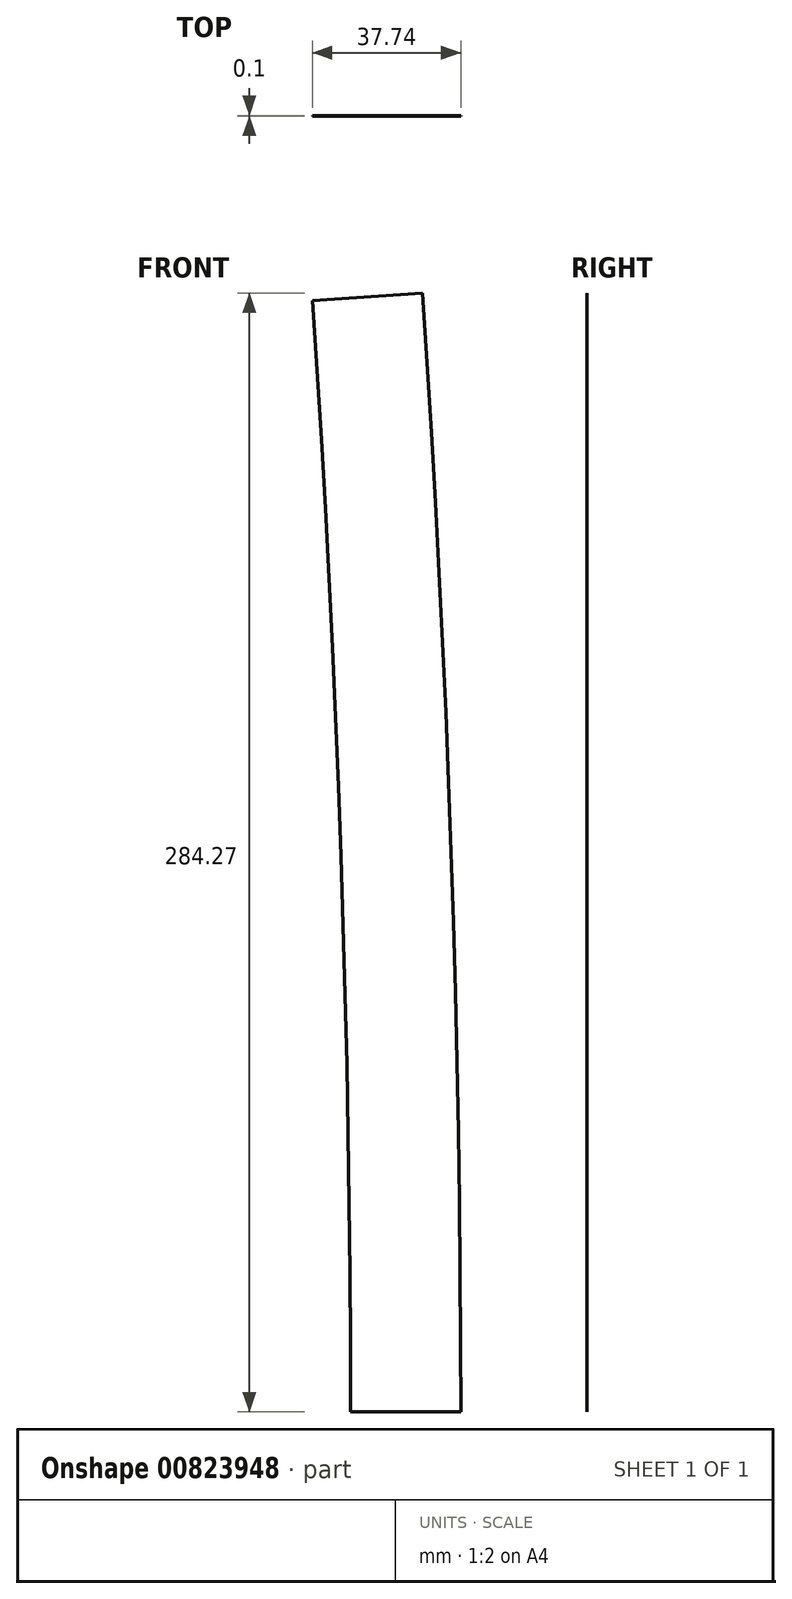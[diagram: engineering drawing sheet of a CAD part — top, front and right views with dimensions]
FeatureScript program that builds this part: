
annotation { "Feature Type Name" : "Feature", "Feature Type Description" : "" }
export const myFeature = defineFeature(function(context is Context, id is Id, definition is map)
    precondition{}
    {
        {
            var Q0;
            Q0=qCreatedBy(makeId("Front.planeOp"),FACE);
            var sketch = newSketch(context, id + "F0", { "sketchPlane" : qUnion([Q0])});
            skLineSegment(sketch, "E0", {"start": v(-28, 0) * mm, "end": v(0, 0) * mm});
            skLineSegment(sketch, "E1", {"start": v(-37.74, 282.38) * mm, "end": v(-9.8, 284.27) * mm});
            skArc(sketch, "E2", {"start": v(0, 0) * mm, "mid": v(-2.45, 142.22) * mm, "end": v(-9.8, 284.27) * mm});
            skArc(sketch, "E3", {"start": v(-28, 0) * mm, "mid": v(-30.43, 141.27) * mm, "end": v(-37.74, 282.38) * mm});
            skPoint(sketch, "E4.startSnap0", {"position": v(-6.85, 237.76) * mm});
            skSolve(sketch);
        }
        {
            var Q0;
            Q0=makeQuery(id+"F0.imprint","IMPRINT",FACE,{"disambiguationData":[TD([[makeQuery(id+"F0.imprint","IMPRINT",EDGE,{"derivedFrom":sQuery(id+"F0.wireOp",EDGE,"E0")}),1.0]])]});
            extrude(context, id + "F1", {"entities" : qUnion([Q0]), "depth" : 0.1 * mm, "offsetDistance" : 25 * mm});
        }
    });
